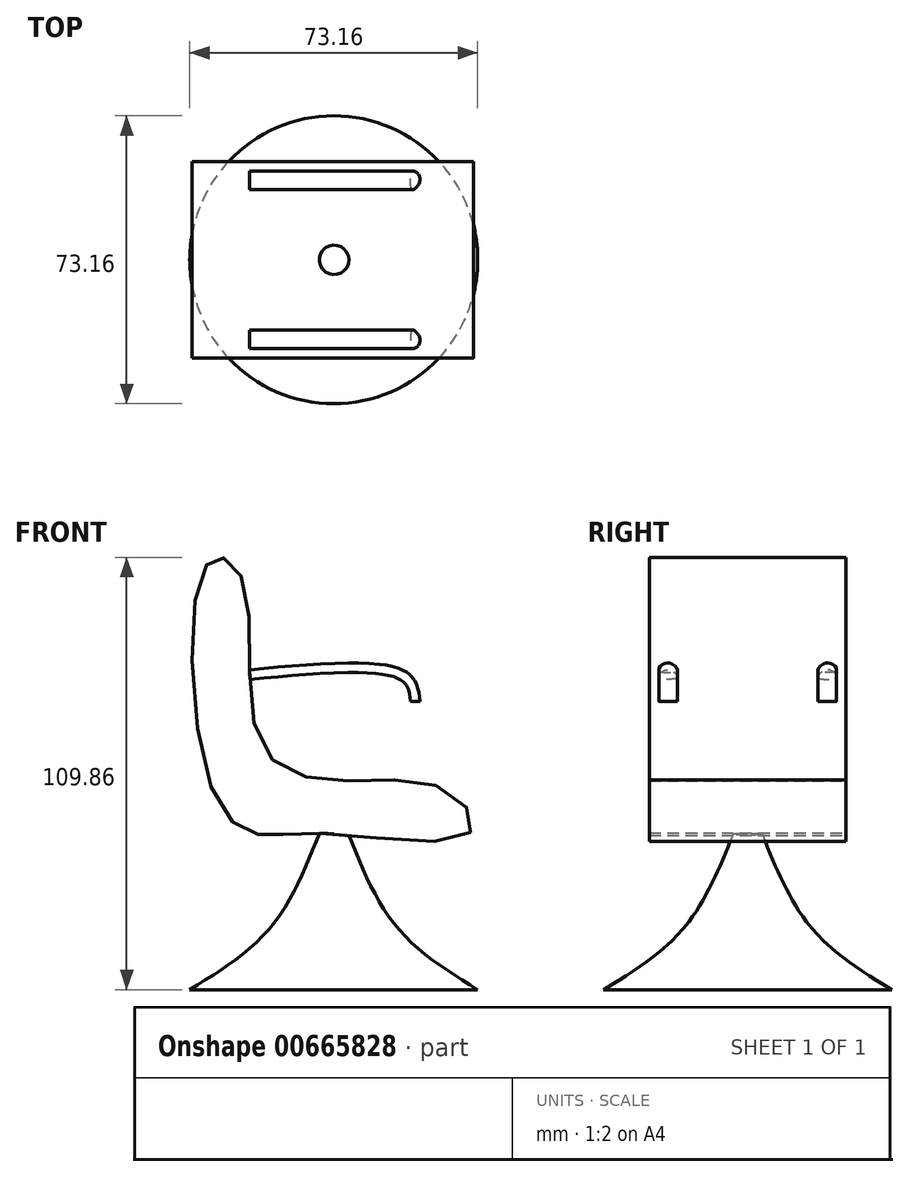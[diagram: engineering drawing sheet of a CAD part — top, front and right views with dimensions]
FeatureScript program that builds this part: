
annotation { "Feature Type Name" : "Feature", "Feature Type Description" : "" }
export const myFeature = defineFeature(function(context is Context, id is Id, definition is map)
    precondition{}
    {
        {
            var Q0;
            Q0=qCreatedBy(makeId("Top.planeOp"),FACE);
            var sketch = newSketch(context, id + "F0", { "sketchPlane" : qUnion([Q0])});
            skCircle(sketch, "E0", {"center": v(0, 0) * mm, "radius": 36.58 * mm});
            skSolve(sketch);
        }
        {
            var Q0;
            Q0=qCreatedBy(makeId("Top.planeOp"),FACE);
            cPlane(context, id + "F1", {"entities" : qUnion([Q0]), "cplaneType" : CPlaneType.OFFSET, "offset" : 15 * mm, "width" : 152.4 * mm, "height" : 152.4 * mm});
        }
        {
            var Q0;
            Q0=qCreatedBy(id+"F1.planeOp",FACE);
            var sketch = newSketch(context, id + "F2", { "sketchPlane" : qUnion([Q0])});
            skCircle(sketch, "E1", {"center": v(0, 0) * mm, "radius": 16.8 * mm});
            skSolve(sketch);
        }
        {
            var Q0;
            Q0=qCreatedBy(id+"F1.planeOp",FACE);
            cPlane(context, id + "F3", {"entities" : qUnion([Q0]), "cplaneType" : CPlaneType.OFFSET, "offset" : 25 * mm, "width" : 150 * mm, "height" : 150 * mm});
        }
        {
            var Q0;
            Q0=qCreatedBy(id+"F3.planeOp",FACE);
            var sketch = newSketch(context, id + "F4", { "sketchPlane" : qUnion([Q0])});
            skCircle(sketch, "E2", {"center": v(0, 0) * mm, "radius": 3.55 * mm});
            skSolve(sketch);
        }
        {
            var Q0;
            Q0=makeQuery(id+"F0.imprint","IMPRINT",FACE,{"disambiguationData":[TD([[makeQuery(id+"F0.imprint","IMPRINT",EDGE,{"derivedFrom":sQuery(id+"F0.wireOp",EDGE,"E0")}),1.0]])]});
            var Q1;
            Q1=makeQuery(id+"F2.imprint","IMPRINT",FACE,{"disambiguationData":[TD([[makeQuery(id+"F2.imprint","IMPRINT",EDGE,{"derivedFrom":sQuery(id+"F2.wireOp",EDGE,"E1")}),1.0]])]});
            var Q2;
            Q2=makeQuery(id+"F4.imprint","IMPRINT",FACE,{"disambiguationData":[TD([[makeQuery(id+"F4.imprint","IMPRINT",EDGE,{"derivedFrom":sQuery(id+"F4.wireOp",EDGE,"E2")}),1.0]])]});
            loft(context, id + "F5", {"sheetProfilesArray" : [{ "sheetProfileEntities" : qUnion([Q0]) }, { "sheetProfileEntities" : qUnion([Q1]) }, { "sheetProfileEntities" : qUnion([Q2]) }]});
        }
        {
            var Q0;
            Q0=qCreatedBy(makeId("Front.planeOp"),FACE);
            var sketch = newSketch(context, id + "F6", { "sketchPlane" : qUnion([Q0])});
            skFitSpline(sketch, "E3", {"points": [v(34.68, 39.94) * mm, v(28.47, 50.84) * mm, v(0, 53.1) * mm, v(-18.89, 63.24) * mm, v(-22.46, 101.96) * mm, v(-28.85, 109.86) * mm, v(-34.3, 103.47) * mm, v(-30.17, 49.15) * mm, v(-18.7, 39.38) * mm, v(-3.85, 39.75) * mm, v(34.68, 39.94) * mm]});
            skSolve(sketch);
        }
        {
            var Q0;
            Q0=makeQuery(id+"F6.imprint","IMPRINT",FACE,{"disambiguationData":[TD([[makeQuery(id+"F6.imprint","IMPRINT",EDGE,{"derivedFrom":sQuery(id+"F6.wireOp",EDGE,"E3")}),1.0]])]});
            extrude(context, id + "F7", {"entities" : qUnion([Q0]), "operationType" : NewBodyOperationType.ADD, "depth" : 25 * mm, "offsetDistance" : 25 * mm});
        }
        {
            var Q0;
            Q0=qCreatedBy(makeId("Front.planeOp"),FACE);
            cPlane(context, id + "F8", {"entities" : qUnion([Q0]), "cplaneType" : CPlaneType.OFFSET, "offset" : 20 * mm, "width" : 150 * mm, "height" : 150 * mm});
        }
        {
            var Q0;
            Q0=qCreatedBy(makeId("Right.planeOp"),FACE);
            cPlane(context, id + "F9", {"entities" : qUnion([Q0]), "cplaneType" : CPlaneType.OFFSET, "offset" : 22 * mm, "oppositeDirection" : true, "width" : 150 * mm, "height" : 150 * mm});
        }
        {
            var Q0;
            Q0=qCreatedBy(id+"F9.planeOp",FACE);
            var sketch = newSketch(context, id + "F10", { "sketchPlane" : qUnion([Q0])});
            skFitSpline(sketch, "E4", {"points": [v(-22.53, 79.27) * mm, v(-22.04, 80.52) * mm, v(-20.71, 81.18) * mm, v(-19.12, 80.84) * mm, v(-17.82, 79.32) * mm, v(-20.13, 78.78) * mm, v(-22.53, 79.27) * mm]});
            skSolve(sketch);
        }
        {
            var Q0;
            Q0=qCreatedBy(id+"F8.planeOp",FACE);
            var sketch = newSketch(context, id + "F11", { "sketchPlane" : qUnion([Q0])});
            skFitSpline(sketch, "E5", {"points": [v(-22.5, 79.88) * mm, v(17.8, 79.6) * mm, v(20.63, 73.26) * mm], "startDerivative": vector(73.76, 7.1) * mm, "endDerivative": vector(2.68, -24.72) * mm});
            skSolve(sketch);
        }
        {
            var Q0;
            Q0 = qSketchRegion(id + "F10", true);
            var Q1;
            Q1 = qConstructionFilter(qBodyType(qCreatedBy(id + "F11" ,EDGE), BodyType.WIRE), ConstructionObject.NO);
            sweep(context, id + "F12", {"operationType" : NewBodyOperationType.ADD, "profiles" : qUnion([Q0]), "path" : qUnion([Q1])});
        }
        {
            var Q0;
            Q0=makeQuery(id+"F5.opLoft","SWEPT_BODY",BODY,{"disambiguationData":[OSD([makeQuery(id+"F0.imprint","IMPRINT",FACE,{"disambiguationData":[TD([[makeQuery(id+"F0.imprint","IMPRINT",EDGE,{"derivedFrom":sQuery(id+"F0.wireOp",EDGE,"E0")}),1.0]])]}),sQuery(id+"F2.wireOp",EDGE,"E1"),makeQuery(id+"F4.imprint","IMPRINT",FACE,{"disambiguationData":[TD([[makeQuery(id+"F4.imprint","IMPRINT",EDGE,{"derivedFrom":sQuery(id+"F4.wireOp",EDGE,"E2")}),1.0]])]})])]});
            var Q1;
            Q1=qCreatedBy(makeId("Front.planeOp"),FACE);
            mirror(context, id + "F13", {"operationType" : NewBodyOperationType.ADD, "entities" : qUnion([Q0]), "mirrorPlane" : qUnion([Q1])});
        }
    });
